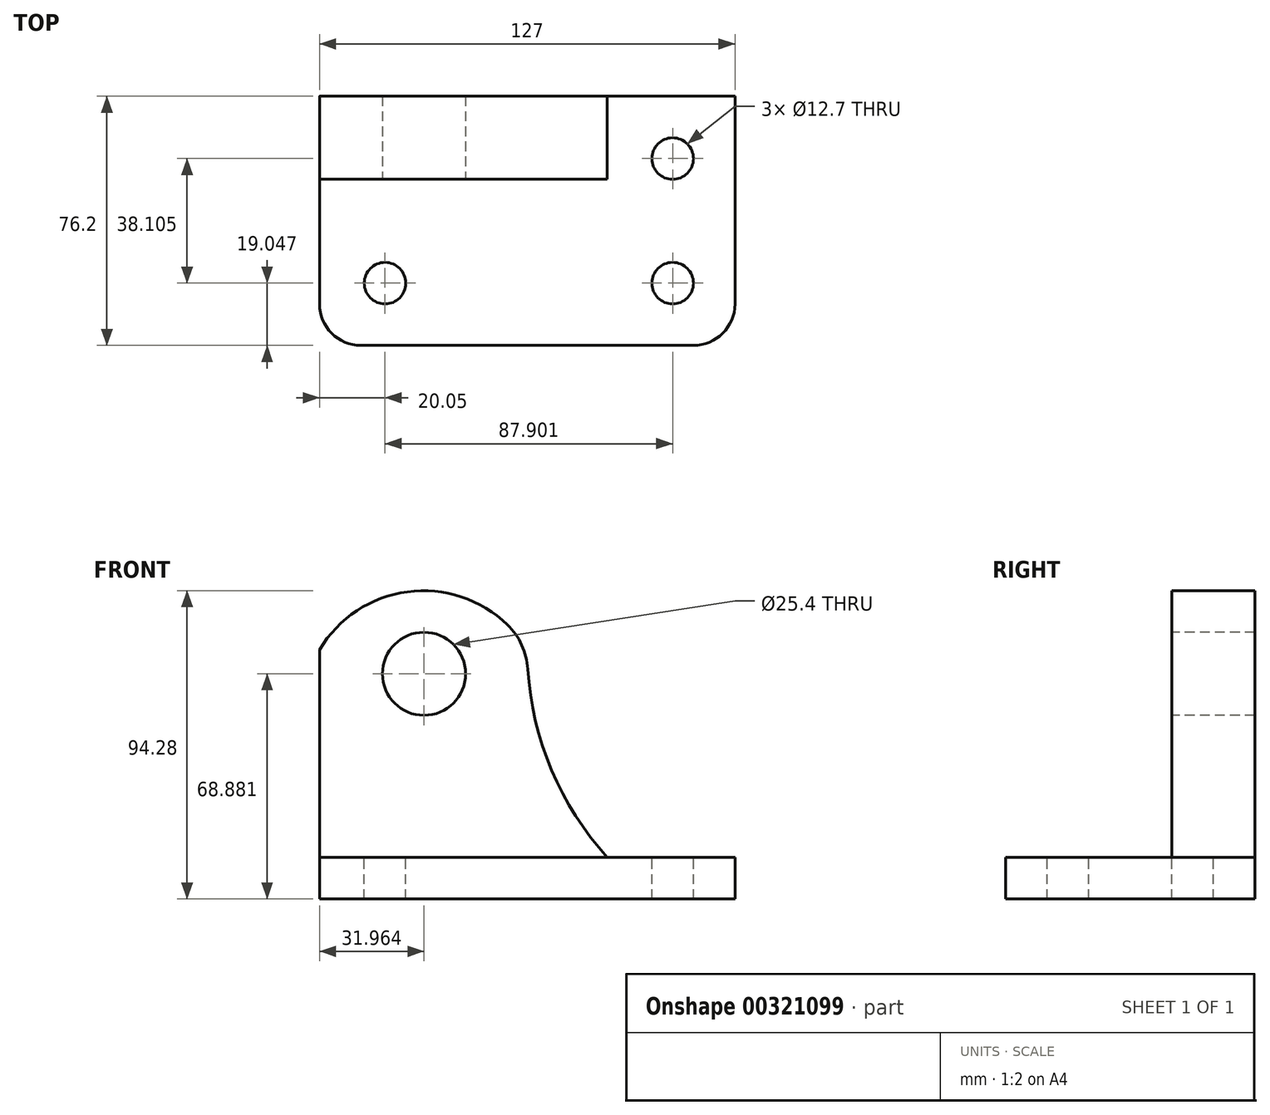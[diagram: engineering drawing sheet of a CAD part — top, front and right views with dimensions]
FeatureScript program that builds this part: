
annotation { "Feature Type Name" : "Feature", "Feature Type Description" : "" }
export const myFeature = defineFeature(function(context is Context, id is Id, definition is map)
    precondition{}
    {
        {
            var Q0;
            Q0=qCreatedBy(makeId("Top.planeOp"),FACE);
            var sketch = newSketch(context, id + "F0", { "sketchPlane" : qUnion([Q0])});
            skLineSegment(sketch, "E0.bottom", {"start": v(-61.75, 42.15) * mm, "end": v(65.25, 42.15) * mm});
            skLineSegment(sketch, "E0.top", {"start": v(-61.75, -34.05) * mm, "end": v(65.25, -34.05) * mm});
            skLineSegment(sketch, "E0.left", {"start": v(-61.75, 42.15) * mm, "end": v(-61.75, -34.05) * mm});
            skLineSegment(sketch, "E0.right", {"start": v(65.25, 42.15) * mm, "end": v(65.25, -34.05) * mm});
            skSolve(sketch);
        }
        {
            var Q0;
            Q0=makeQuery(id+"F0.imprint","IMPRINT",FACE,{"disambiguationData":[TD([[makeQuery(id+"F0.imprint","IMPRINT",EDGE,{"derivedFrom":sQuery(id+"F0.wireOp",EDGE,"E0.bottom")}),-1.0]])]});
            extrude(context, id + "F1", {"entities" : qUnion([Q0]), "depth" : 12.7 * mm});
        }
        {
            var Q0;
            Q0=makeQuery(id+"F1.opExtrude","SWEPT_EDGE",EDGE,{"disambiguationData":[OSD([sQuery(id+"F0.wireOp",EDGE,"E0.top"),sQuery(id+"F0.wireOp",EDGE,"E0.left")])]});
            fillet(context, id + "F2", {"entities" : qUnion([Q0]), "radius" : 12.7 * mm, "tangentPropagation" : true, "allowEdgeOverflow" : false});
        }
        {
            var Q0;
            Q0=makeQuery(id+"F1.opExtrude","SWEPT_EDGE",EDGE,{"disambiguationData":[OSD([sQuery(id+"F0.wireOp",EDGE,"E0.top"),sQuery(id+"F0.wireOp",EDGE,"E0.right")])]});
            fillet(context, id + "F3", {"entities" : qUnion([Q0]), "radius" : 12.7 * mm, "tangentPropagation" : true, "allowEdgeOverflow" : false});
        }
        {
            var Q0;
            Q0=makeQuery(id+"F1.opExtrude","CAP_FACE",FACE,{"disambiguationData":[OSD([sQuery(id+"F0.wireOp",EDGE,"E0.bottom"),sQuery(id+"F0.wireOp",EDGE,"E0.top"),sQuery(id+"F0.wireOp",EDGE,"E0.left"),sQuery(id+"F0.wireOp",EDGE,"E0.right")])],"isStart":false});
            var sketch = newSketch(context, id + "F4", { "sketchPlane" : qUnion([Q0])});
            skLineSegment(sketch, "E1.bottom", {"start": v(-61.75, 42.15) * mm, "end": v(1.75, 42.15) * mm});
            skLineSegment(sketch, "E1.top", {"start": v(-61.75, 16.75) * mm, "end": v(1.75, 16.75) * mm});
            skLineSegment(sketch, "E1.left", {"start": v(-61.75, 42.15) * mm, "end": v(-61.75, 16.75) * mm});
            skLineSegment(sketch, "E1.right", {"start": v(1.75, 42.15) * mm, "end": v(1.75, 16.75) * mm});
            skSolve(sketch);
        }
        {
            var Q0;
            Q0=makeQuery(id+"F4.imprint","IMPRINT",FACE,{"disambiguationData":[TD([[makeQuery(id+"F4.imprint","IMPRINT",EDGE,{"derivedFrom":sQuery(id+"F4.wireOp",EDGE,"E1.bottom")}),-1.0]])]});
            extrude(context, id + "F5", {"entities" : qUnion([Q0]), "operationType" : NewBodyOperationType.ADD, "depth" : 63.5 * mm});
        }
        {
            var Q0;
            Q0=makeQuery(id+"F5.opExtrude","SWEPT_FACE",FACE,{"disambiguationData":[OSD([sQuery(id+"F4.wireOp",EDGE,"E1.top")])]});
            var sketch = newSketch(context, id + "F6", { "sketchPlane" : qUnion([Q0])});
            skArc(sketch, "E2", {"start": v(1.75, 76.2) * mm, "mid": v(-30, 94.28) * mm, "end": v(-61.75, 76.2) * mm});
            skArc(sketch, "E3", {"start": v(1.75, 76.2) * mm, "mid": v(8.09, 42.17) * mm, "end": v(26.25, 12.7) * mm});
            skLineSegment(sketch, "E4", {"start": v(26.25, 12.7) * mm, "end": v(1.75, 12.7) * mm});
            skLineSegment(sketch, "E5", {"start": v(1.75, 12.7) * mm, "end": v(1.75, 76.2) * mm});
            skSolve(sketch);
        }
        {
            var Q0;
            Q0=makeQuery(id+"F6.imprint","IMPRINT",FACE,{"disambiguationData":[TD([[makeQuery(id+"F6.imprint","IMPRINT",EDGE,{"derivedFrom":sQuery(id+"F6.wireOp",EDGE,"E2")}),1.0]])]});
            extrude(context, id + "F7", {"entities" : qUnion([Q0]), "operationType" : NewBodyOperationType.ADD, "oppositeDirection" : true, "depth" : 25.4 * mm});
        }
        {
            var Q0;
            Q0=makeQuery(id+"F6.imprint","IMPRINT",FACE,{"disambiguationData":[TD([[makeQuery(id+"F6.imprint","IMPRINT",EDGE,{"derivedFrom":sQuery(id+"F6.wireOp",EDGE,"E3")}),-1.0]])]});
            extrude(context, id + "F8", {"entities" : qUnion([Q0]), "operationType" : NewBodyOperationType.ADD, "oppositeDirection" : true, "depth" : 25.4 * mm});
        }
        {
            var Q0;
            {var subQ0=sQuery(id+"F6.wireOp",EDGE,"E5");var subQ1=sQuery(id+"F6.wireOp",EDGE,"E3");var subQ2=sQuery(id+"F6.wireOp",EDGE,"E2");var subQ3=sQuery(id+"F4.wireOp",EDGE,"E1.top");Q0=makeQuery(id+"F8.boolean.opBoolean","MERGE",EDGE,{"derivedFrom":[makeQuery(id+"F7.boolean.opBoolean","MERGE",EDGE,{"derivedFrom":[makeQuery(id+"F5.opExtrude","CAP_EDGE",EDGE,{"disambiguationData":[OSD([sQuery(id+"F4.wireOp",EDGE,"E1.right")])],"isStart":false}),makeQuery(id+"F7.opExtrude","SWEPT_EDGE",EDGE,{"disambiguationData":[OSD([subQ3,subQ2,subQ1,subQ0])]})]}),makeQuery(id+"F8.opExtrude","SWEPT_EDGE",EDGE,{"disambiguationData":[OSD([subQ3,subQ2,subQ1,subQ0])]})]});}
            fillet(context, id + "F9", {"entities" : qUnion([Q0]), "radius" : 20.64 * mm, "tangentPropagation" : true, "allowEdgeOverflow" : false});
        }
        {
            var Q0;
            Q0=makeQuery(id+"F6.imprint","IMPRINT",FACE,{"disambiguationData":[TD([[makeQuery(id+"F6.imprint","IMPRINT",EDGE,{"derivedFrom":sQuery(id+"F6.wireOp",EDGE,"E5")}),-1.0]])]});
            var sketch = newSketch(context, id + "F10", { "sketchPlane" : qUnion([Q0])});
            skCircle(sketch, "E6", {"center": v(-29.79, 68.88) * mm, "radius": 12.7 * mm});
            skSolve(sketch);
        }
        {
            var Q0;
            {var subQ0=sQuery(id+"F10.wireOp",EDGE,"E6");var subQ1=makeQuery(id+"F6.imprint","IMPRINT",EDGE,{"derivedFrom":makeQuery(id+"F5.opExtrude","CAP_EDGE",EDGE,{"disambiguationData":[OSD([sQuery(id+"F4.wireOp",EDGE,"E1.top")])],"isStart":false})});var subQ2=makeQuery(id+"F10.imprint","INTERSECT",VERTEX,{"disambiguationData":[OD(0.0)],"derivedFrom":[subQ1,subQ0]});Q0=makeQuery(id+"F10.imprint","IMPRINT",FACE,{"disambiguationData":[TD([[makeQuery(id+"F10.imprint","IMPRINT",EDGE,{"disambiguationData":[TD([[subQ2,-1.0]])],"derivedFrom":subQ0}),1.0]])]});}
            extrude(context, id + "F11", {"entities" : qUnion([Q0]), "operationType" : NewBodyOperationType.REMOVE, "endBound" : BoundingType.THROUGH_ALL, "oppositeDirection" : true, "depth" : 25.4 * mm});
        }
        {
            var Q0;
            {var subQ0=sQuery(id+"F10.wireOp",EDGE,"E6");var subQ1=makeQuery(id+"F6.imprint","IMPRINT",EDGE,{"derivedFrom":makeQuery(id+"F5.opExtrude","CAP_EDGE",EDGE,{"disambiguationData":[OSD([sQuery(id+"F4.wireOp",EDGE,"E1.top")])],"isStart":false})});var subQ2=makeQuery(id+"F10.imprint","INTERSECT",VERTEX,{"disambiguationData":[OD(0.0)],"derivedFrom":[subQ1,subQ0]});Q0=makeQuery(id+"F10.imprint","IMPRINT",FACE,{"disambiguationData":[TD([[makeQuery(id+"F10.imprint","IMPRINT",EDGE,{"disambiguationData":[TD([[subQ2,1.0]])],"derivedFrom":subQ0}),1.0]])]});}
            extrude(context, id + "F12", {"entities" : qUnion([Q0]), "operationType" : NewBodyOperationType.REMOVE, "endBound" : BoundingType.THROUGH_ALL, "oppositeDirection" : true, "depth" : 25.4 * mm});
        }
        {
            var Q0;
            {var subQ0=sQuery(id+"F4.wireOp",EDGE,"E1.left");Q0=makeQuery(id+"F7.boolean.opBoolean","MERGE",EDGE,{"derivedFrom":[makeQuery(id+"F5.opExtrude","CAP_EDGE",EDGE,{"disambiguationData":[OSD([subQ0])],"isStart":false}),makeQuery(id+"F7.opExtrude","SWEPT_EDGE",EDGE,{"disambiguationData":[OSD([sQuery(id+"F0.wireOp",EDGE,"E0.left"),sQuery(id+"F4.wireOp",EDGE,"E1.top"),subQ0,sQuery(id+"F6.wireOp",EDGE,"E2")])]})]});}
            fillet(context, id + "F13", {"entities" : qUnion([Q0]), "radius" : 0.27 * mm, "tangentPropagation" : true, "allowEdgeOverflow" : false});
        }
        {
            var Q0;
            Q0=makeQuery(id+"F1.opExtrude","CAP_FACE",FACE,{"disambiguationData":[OSD([sQuery(id+"F0.wireOp",EDGE,"E0.bottom"),sQuery(id+"F0.wireOp",EDGE,"E0.top"),sQuery(id+"F0.wireOp",EDGE,"E0.left"),sQuery(id+"F0.wireOp",EDGE,"E0.right")])],"isStart":false});
            var sketch = newSketch(context, id + "F14", { "sketchPlane" : qUnion([Q0])});
            skCircle(sketch, "E7", {"center": v(-41.7, -15) * mm, "radius": 6.35 * mm});
            skCircle(sketch, "E8", {"center": v(46.2, -15) * mm, "radius": 6.35 * mm});
            skCircle(sketch, "E9", {"center": v(46.2, 23.1) * mm, "radius": 6.35 * mm});
            skSolve(sketch);
        }
        {
            var Q0;
            Q0=makeQuery(id+"F14.imprint","IMPRINT",FACE,{"disambiguationData":[TD([[makeQuery(id+"F14.imprint","IMPRINT",EDGE,{"derivedFrom":sQuery(id+"F14.wireOp",EDGE,"E7")}),1.0]])]});
            extrude(context, id + "F15", {"entities" : qUnion([Q0]), "operationType" : NewBodyOperationType.REMOVE, "endBound" : BoundingType.THROUGH_ALL, "oppositeDirection" : true, "depth" : 25.4 * mm});
        }
        {
            var Q0;
            Q0=makeQuery(id+"F14.imprint","IMPRINT",FACE,{"disambiguationData":[TD([[makeQuery(id+"F14.imprint","IMPRINT",EDGE,{"derivedFrom":sQuery(id+"F14.wireOp",EDGE,"E8")}),1.0]])]});
            extrude(context, id + "F16", {"entities" : qUnion([Q0]), "operationType" : NewBodyOperationType.REMOVE, "endBound" : BoundingType.THROUGH_ALL, "oppositeDirection" : true, "depth" : 25.4 * mm});
        }
        {
            var Q0;
            Q0=makeQuery(id+"F14.imprint","IMPRINT",FACE,{"disambiguationData":[TD([[makeQuery(id+"F14.imprint","IMPRINT",EDGE,{"derivedFrom":sQuery(id+"F14.wireOp",EDGE,"E9")}),1.0]])]});
            extrude(context, id + "F17", {"entities" : qUnion([Q0]), "operationType" : NewBodyOperationType.REMOVE, "endBound" : BoundingType.THROUGH_ALL, "oppositeDirection" : true, "depth" : 25.4 * mm});
        }
    });
